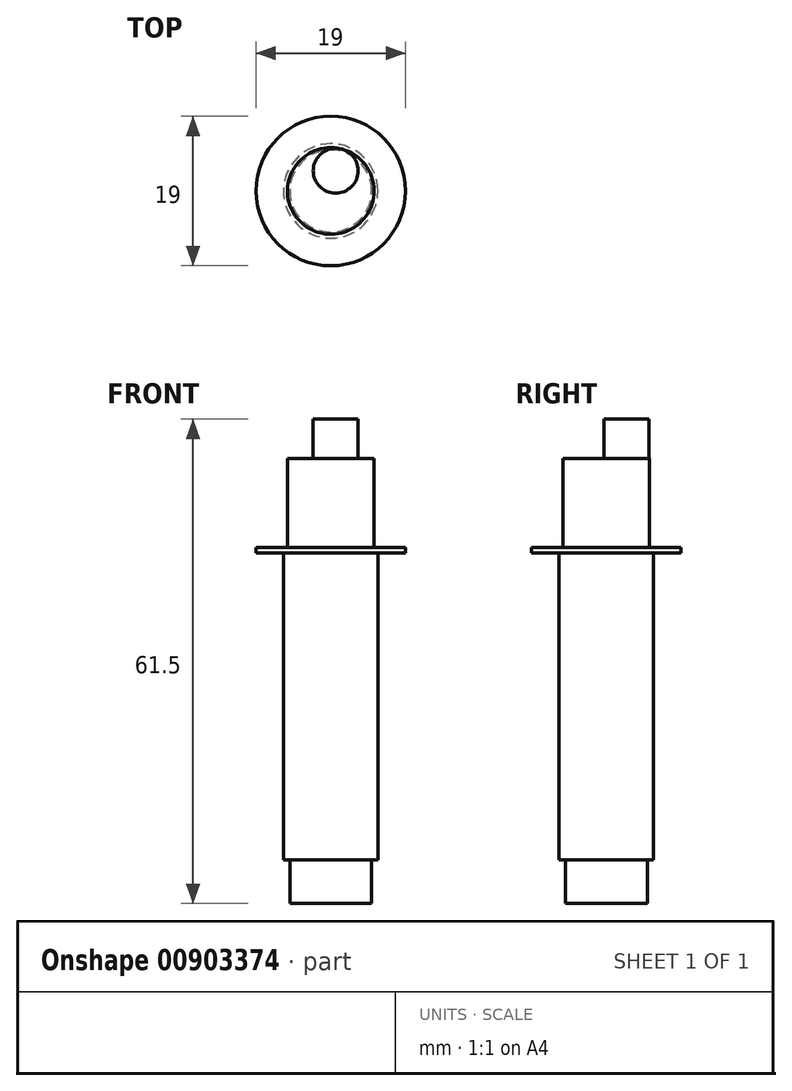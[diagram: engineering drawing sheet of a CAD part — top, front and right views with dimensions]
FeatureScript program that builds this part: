
annotation { "Feature Type Name" : "Feature", "Feature Type Description" : "" }
export const myFeature = defineFeature(function(context is Context, id is Id, definition is map)
    precondition{}
    {
        {
            var Q0;
            Q0=qCreatedBy(makeId("Top.planeOp"),FACE);
            var sketch = newSketch(context, id + "F0", { "sketchPlane" : qUnion([Q0])});
            skCircle(sketch, "E0", {"center": v(0, 0) * mm, "radius": 6 * mm});
            skSolve(sketch);
        }
        {
            var Q0;
            Q0 = qSketchRegion(id + "F0", true);
            extrude(context, id + "F1", {"entities" : qUnion([Q0]), "depth" : 39 * mm, "offsetDistance" : 25 * mm});
        }
        {
            var Q0;
            Q0=makeQuery(id+"F1.opExtrude","CAP_FACE",FACE,{"disambiguationData":[OSD([sQuery(id+"F0.wireOp",EDGE,"E0")])],"isStart":false});
            var sketch = newSketch(context, id + "F2", { "sketchPlane" : qUnion([Q0])});
            skCircle(sketch, "E1", {"center": v(0, 0) * mm, "radius": 5.5 * mm});
            skSolve(sketch);
        }
        {
            var Q0;
            Q0 = qSketchRegion(id + "F2", true);
            extrude(context, id + "F3", {"entities" : qUnion([Q0]), "operationType" : NewBodyOperationType.ADD, "depth" : 12 * mm, "offsetDistance" : 25 * mm});
        }
        {
            var Q0;
            Q0=makeQuery(id+"F1.opExtrude","CAP_FACE",FACE,{"disambiguationData":[OSD([sQuery(id+"F0.wireOp",EDGE,"E0")])],"isStart":true});
            var sketch = newSketch(context, id + "F4", { "sketchPlane" : qUnion([Q0])});
            skCircle(sketch, "E2", {"center": v(0, 0) * mm, "radius": 5.2 * mm});
            skSolve(sketch);
        }
        {
            var Q0;
            Q0 = qSketchRegion(id + "F4", true);
            extrude(context, id + "F5", {"entities" : qUnion([Q0]), "depth" : 5.5 * mm, "offsetDistance" : 25 * mm});
        }
        {
            var Q0;
            Q0=makeQuery(id+"F3.opExtrude","CAP_FACE",FACE,{"disambiguationData":[OSD([sQuery(id+"F2.wireOp",EDGE,"E1")])],"isStart":false});
            var sketch = newSketch(context, id + "F6", { "sketchPlane" : qUnion([Q0])});
            skCircle(sketch, "E3", {"center": v(0.63, 2.57) * mm, "radius": 2.85 * mm});
            skSolve(sketch);
        }
        {
            var Q0;
            Q0 = qSketchRegion(id + "F6", true);
            extrude(context, id + "F7", {"entities" : qUnion([Q0]), "depth" : 5 * mm, "offsetDistance" : 25 * mm});
        }
        {
            var Q0;
            Q0=makeQuery(id+"F1.opExtrude","CAP_FACE",FACE,{"disambiguationData":[OSD([sQuery(id+"F0.wireOp",EDGE,"E0")])],"isStart":false});
            var sketch = newSketch(context, id + "F8", { "sketchPlane" : qUnion([Q0])});
            skCircle(sketch, "E4", {"center": v(0, 0) * mm, "radius": 9.5 * mm});
            skSolve(sketch);
        }
        {
            var Q0;
            Q0 = qSketchRegion(id + "F8", true);
            extrude(context, id + "F9", {"entities" : qUnion([Q0]), "operationType" : NewBodyOperationType.ADD, "depth" : .7 * mm, "offsetDistance" : 25 * mm});
        }
    });
